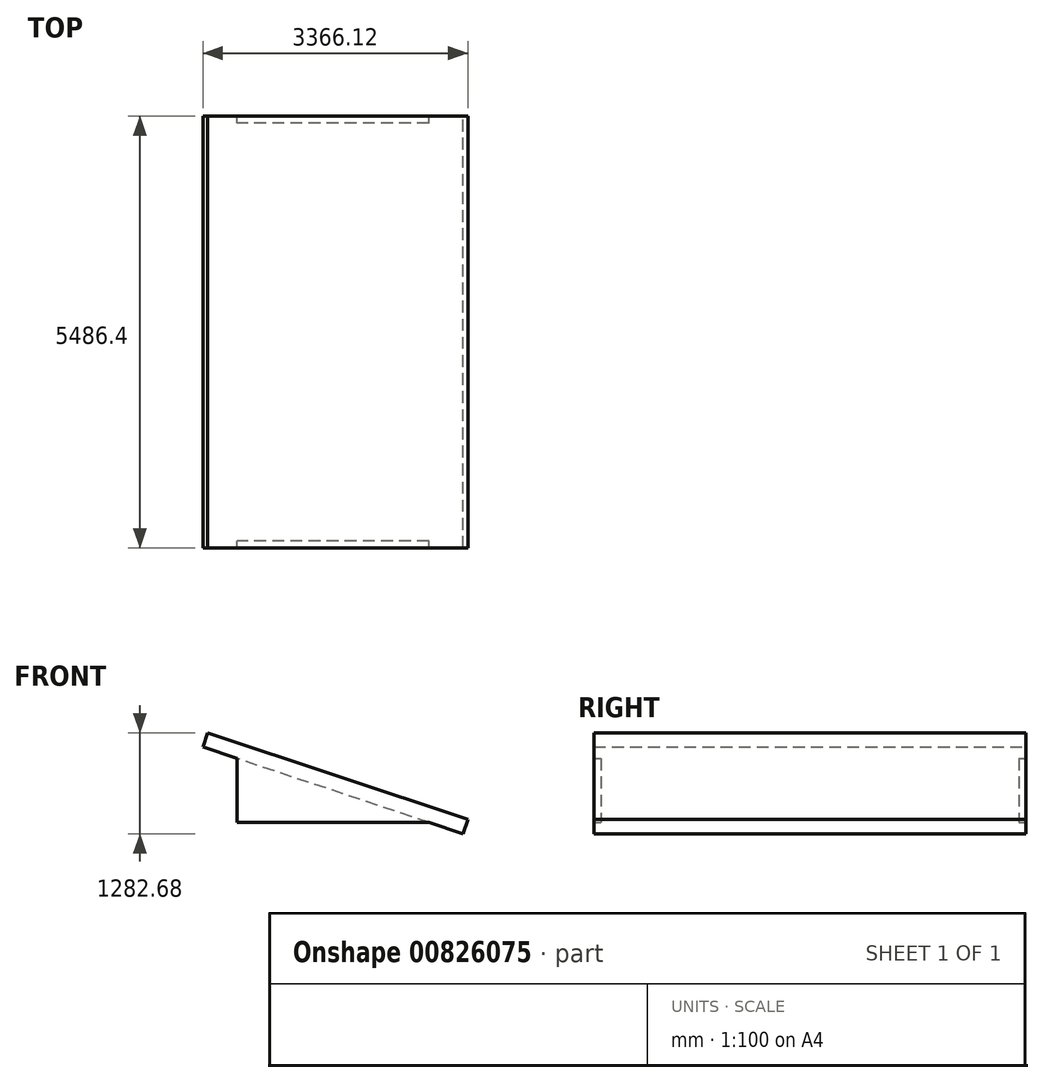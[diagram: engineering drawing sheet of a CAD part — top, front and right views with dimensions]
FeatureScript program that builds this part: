
annotation { "Feature Type Name" : "Feature", "Feature Type Description" : "" }
export const myFeature = defineFeature(function(context is Context, id is Id, definition is map)
    precondition{}
    {
        {
            var Q0;
            Q0=qCreatedBy(makeId("Front.planeOp"),FACE);
            var sketch = newSketch(context, id + "F0", { "sketchPlane" : qUnion([Q0])});
            skLineSegment(sketch, "E0.bottom", {"start": v(0, 0) * mm, "end": v(2438.4, 0) * mm});
            skLineSegment(sketch, "E0.left", {"start": v(0, 0) * mm, "end": v(0, 812.8) * mm});
            skLineSegment(sketch, "E1", {"start": v(-433.74, 957.38) * mm, "end": v(2872.14, -144.58) * mm});
            skLineSegment(sketch, "E2.0", {"start": v(-373.5, 1138.1) * mm, "end": v(2932.38, 36.14) * mm});
            skLineSegment(sketch, "E3", {"start": v(2438.4, 0) * mm, "end": v(2498.64, 180.72) * mm});
            skLineSegment(sketch, "E4", {"start": v(0, 812.8) * mm, "end": v(60.24, 993.52) * mm});
            skLineSegment(sketch, "E5.0", {"start": v(2872.14, -144.58) * mm, "end": v(2932.38, 36.14) * mm});
            skLineSegment(sketch, "E6.0", {"start": v(-433.74, 957.38) * mm, "end": v(-373.5, 1138.1) * mm});
            skSolve(sketch);
        }
        {
            var Q0;
            {var subQ0=sQuery(id+"F0.wireOp",EDGE,"E4");Q0=makeQuery(id+"F0.imprint","IMPRINT",FACE,{"disambiguationData":[TD([[makeQuery(id+"F0.imprint","IMPRINT",EDGE,{"derivedFrom":subQ0}),1.0]])]});}
            var Q1;
            {var subQ0=sQuery(id+"F0.wireOp",EDGE,"E3");Q1=makeQuery(id+"F0.imprint","IMPRINT",FACE,{"disambiguationData":[TD([[makeQuery(id+"F0.imprint","IMPRINT",EDGE,{"derivedFrom":subQ0}),1.0]])]});}
            var Q2;
            {var subQ0=sQuery(id+"F0.wireOp",EDGE,"E3");Q2=makeQuery(id+"F0.imprint","IMPRINT",FACE,{"disambiguationData":[TD([[makeQuery(id+"F0.imprint","IMPRINT",EDGE,{"derivedFrom":subQ0}),-1.0]])]});}
            var Q3;
            {var subQ0=sQuery(id+"F0.wireOp",EDGE,"E0.bottom");Q3=makeQuery(id+"F0.imprint","IMPRINT",FACE,{"disambiguationData":[TD([[makeQuery(id+"F0.imprint","IMPRINT",EDGE,{"derivedFrom":subQ0}),1.0]])]});}
            extrude(context, id + "F1", {"entities" : qUnion([Q0, Q1, Q2, Q3]), "depth" : 5486.4 * mm, "offsetDistance" : 25.4 * mm});
        }
        {
            var Q0;
            Q0=makeQuery(id+"F1.opExtrude","SWEPT_FACE",FACE,{"disambiguationData":[OSD([sQuery(id+"F0.wireOp",EDGE,"E6.0")])]});
            var sketch = newSketch(context, id + "F2", { "sketchPlane" : qUnion([Q0])});
            skLineSegment(sketch, "E7.bottom", {"start": v(88.9, 771.09) * mm, "end": v(5397.5, 771.09) * mm});
            skLineSegment(sketch, "E7.top", {"start": v(88.9, -41.71) * mm, "end": v(5397.5, -41.71) * mm});
            skLineSegment(sketch, "E7.left", {"start": v(88.9, 771.09) * mm, "end": v(88.9, -41.71) * mm});
            skLineSegment(sketch, "E7.right", {"start": v(5397.5, 771.09) * mm, "end": v(5397.5, -41.71) * mm});
            skSolve(sketch);
        }
        {
            var Q0;
            Q0=qSketchRegion(id+"F2",true);
            extrude(context, id + "F3", {"entities" : qUnion([Q0]), "operationType" : NewBodyOperationType.REMOVE, "oppositeDirection" : true, "depth" : 3352.8 * mm, "offsetDistance" : 25.4 * mm});
        }
    });
